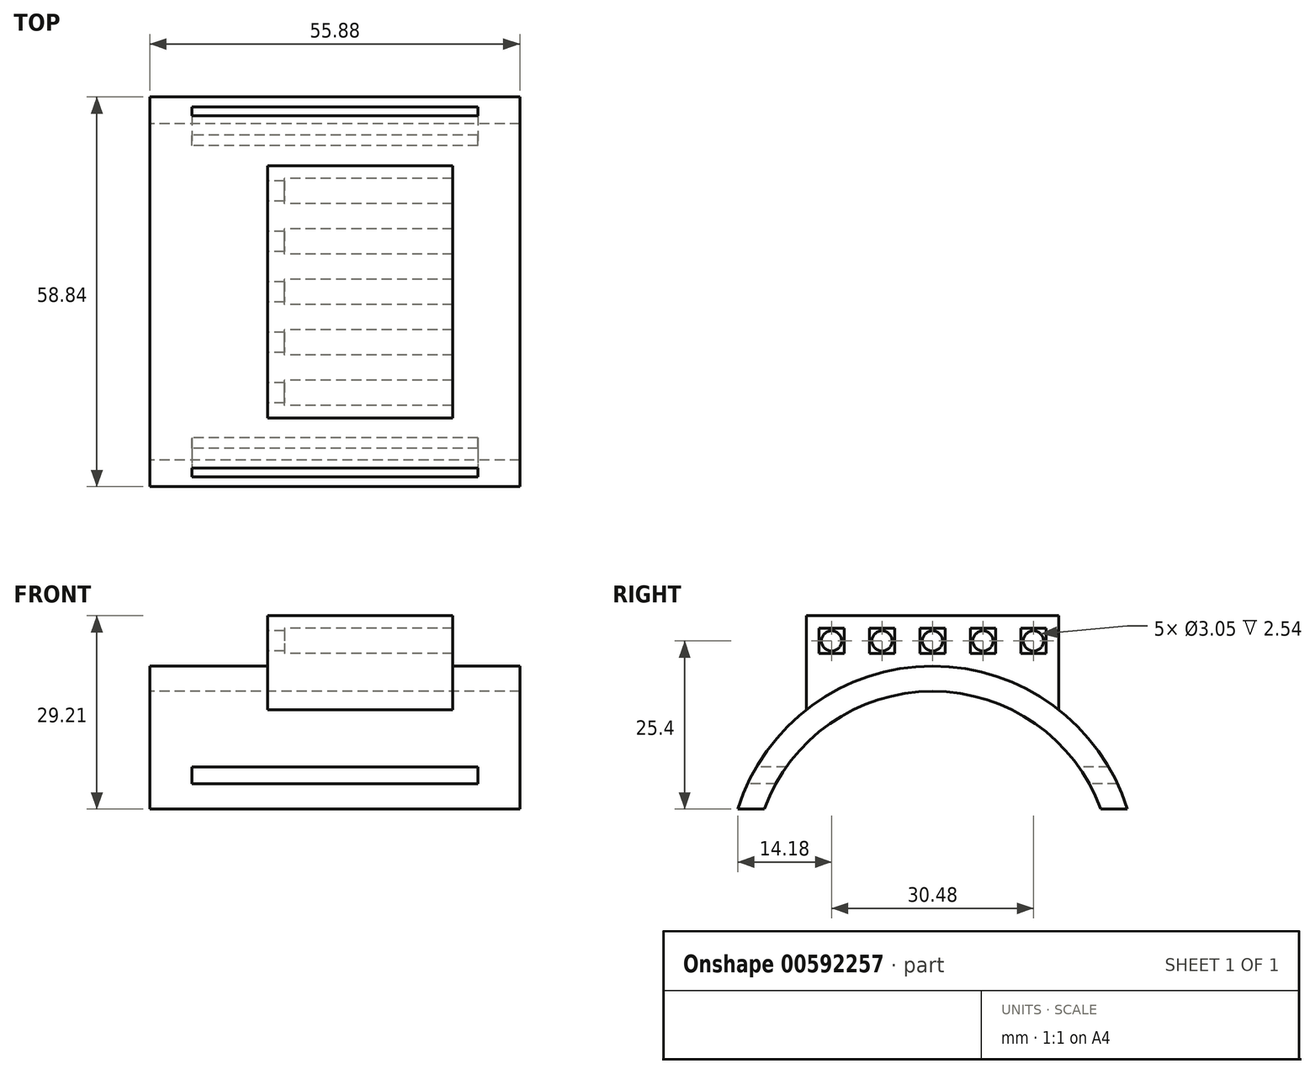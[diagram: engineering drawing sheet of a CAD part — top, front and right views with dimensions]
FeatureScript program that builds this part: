
annotation { "Feature Type Name" : "Feature", "Feature Type Description" : "" }
export const myFeature = defineFeature(function(context is Context, id is Id, definition is map)
    precondition{}
    {
        {
            var Q0;
            Q0=qCreatedBy(makeId("Right.planeOp"),FACE);
            var sketch = newSketch(context, id + "F0", { "sketchPlane" : qUnion([Q0])});
            skLineSegment(sketch, "E0", {"start": v(0, 0) * mm, "end": v(50.8, 0) * mm});
            skLineSegment(sketch, "E1", {"start": v(25.4, 0) * mm, "end": v(25.4, 17.78) * mm});
            skArc(sketch, "E2", {"start": v(50.8, 0) * mm, "mid": v(25.4, 17.78) * mm, "end": v(0, 0) * mm});
            skLineSegment(sketch, "E3", {"start": v(0, 0) * mm, "end": v(-4.02, 0) * mm});
            skLineSegment(sketch, "E4.MirrorCS", {"start": v(50.8, 0) * mm, "end": v(54.82, 0) * mm});
            skArc(sketch, "E5.0", {"start": v(54.82, 0) * mm, "mid": v(25.4, 21.6) * mm, "end": v(-4.02, 0) * mm});
            skPoint(sketch, "E6.orphan", {"position": v(-3.81, 0) * mm});
            skPoint(sketch, "E7.orphan", {"position": v(54.61, 0) * mm});
            skSolve(sketch);
        }
        {
            var Q0;
            {var subQ1=sQuery(id+"F0.wireOp",EDGE,"E3");Q0=makeQuery(id+"F0.imprint","IMPRINT",FACE,{"disambiguationData":[TD([[makeQuery(id+"F0.imprint","IMPRINT",EDGE,{"derivedFrom":subQ1}),-1.0]])]});}
            extrude(context, id + "F1", {"entities" : qUnion([Q0]), "depth" : 55.88 * mm, "offsetDistance" : 25.4 * mm});
        }
        {
            var Q0;
            Q0=makeQuery(id+"F1.opExtrude","CAP_FACE",FACE,{"disambiguationData":[OSD([sQuery(id+"F0.wireOp",EDGE,"E2"),sQuery(id+"F0.wireOp",EDGE,"E3"),sQuery(id+"F0.wireOp",EDGE,"E4.MirrorCS"),sQuery(id+"F0.wireOp",EDGE,"E5.0")])],"isStart":true});
            cPlane(context, id + "F2", {"entities" : qUnion([Q0]), "cplaneType" : CPlaneType.OFFSET, "offset" : 17.78 * mm, "oppositeDirection" : true, "width" : 152.4 * mm, "height" : 152.4 * mm});
        }
        {
            var Q0;
            Q0=qCreatedBy(id+"F2.planeOp",FACE);
            var sketch = newSketch(context, id + "F3", { "sketchPlane" : qUnion([Q0])});
            skLineSegment(sketch, "E8", {"start": v(0, 0) * mm, "end": v(-25.4, 0) * mm});
            skLineSegment(sketch, "E9", {"start": v(-25.4, 0) * mm, "end": v(-25.4, 21.59) * mm});
            skLineSegment(sketch, "E10", {"start": v(-25.4, 21.59) * mm, "end": v(-25.4, 29.21) * mm});
            skCircle(sketch, "E11", {"center": v(-25.4, 25.4) * mm, "radius": 1.52 * mm});
            skCircle(sketch, "E12.1.0.0", {"center": v(-17.78, 25.4) * mm, "radius": 1.52 * mm});
            skCircle(sketch, "E12.2.0.0", {"center": v(-10.16, 25.4) * mm, "radius": 1.52 * mm});
            skLineSegment(sketch, "E12.direction1", {"start": v(-25.4, 25.4) * mm, "end": v(-17.78, 25.4) * mm, "construction": true});
            skCircle(sketch, "E13.1.0.0", {"center": v(-33.02, 25.4) * mm, "radius": 1.52 * mm});
            skCircle(sketch, "E13.2.0.0", {"center": v(-40.64, 25.4) * mm, "radius": 1.52 * mm});
            skLineSegment(sketch, "E13.direction1", {"start": v(-25.4, 25.4) * mm, "end": v(-33.02, 25.4) * mm, "construction": true});
            skLineSegment(sketch, "E14", {"start": v(-6.35, 29.21) * mm, "end": v(-25.4, 29.21) * mm});
            skLineSegment(sketch, "E15", {"start": v(-6.35, 29.2) * mm, "end": v(-6.35, 13.97) * mm});
            skLineSegment(sketch, "E16", {"start": v(-6.35, 13.97) * mm, "end": v(-25.4, 13.97) * mm});
            skLineSegment(sketch, "E17.MirrorCS", {"start": v(-44.45, 13.97) * mm, "end": v(-25.4, 13.97) * mm});
            skLineSegment(sketch, "E18.MirrorCS", {"start": v(-44.45, 29.2) * mm, "end": v(-44.45, 13.97) * mm});
            skLineSegment(sketch, "E19.MirrorCS", {"start": v(-44.45, 29.21) * mm, "end": v(-25.4, 29.21) * mm});
            skArc(sketch, "E20", {"start": v(-6.35, 13.97) * mm, "mid": v(-25.4, 21.59) * mm, "end": v(-44.45, 13.97) * mm});
            skSolve(sketch);
        }
        {
            var Q0;
            Q0=makeQuery(id+"F3.imprint","IMPRINT",FACE,{"disambiguationData":[TD([[makeQuery(id+"F3.imprint","IMPRINT",EDGE,{"derivedFrom":sQuery(id+"F3.wireOp",EDGE,"E13.1.0.0")}),-1.0]])]});
            var Q1;
            Q1=makeQuery(id+"F3.imprint","IMPRINT",FACE,{"disambiguationData":[TD([[makeQuery(id+"F3.imprint","IMPRINT",EDGE,{"derivedFrom":sQuery(id+"F3.wireOp",EDGE,"E12.1.0.0")}),-1.0]])]});
            extrude(context, id + "F4", {"entities" : qUnion([Q0, Q1]), "operationType" : NewBodyOperationType.ADD, "oppositeDirection" : true, "depth" : 2.54 * mm, "offsetDistance" : 25.4 * mm});
        }
        {
            var Q0;
            Q0=qCreatedBy(makeId("Front.planeOp"),FACE);
            var sketch = newSketch(context, id + "F5", { "sketchPlane" : qUnion([Q0])});
            skLineSegment(sketch, "E21.bottom", {"start": v(6.35, 6.35) * mm, "end": v(49.53, 6.35) * mm});
            skLineSegment(sketch, "E21.top", {"start": v(6.35, 3.81) * mm, "end": v(49.53, 3.81) * mm});
            skLineSegment(sketch, "E21.left", {"start": v(6.35, 6.35) * mm, "end": v(6.35, 3.8) * mm});
            skLineSegment(sketch, "E21.right", {"start": v(49.53, 6.35) * mm, "end": v(49.53, 3.81) * mm});
            skSolve(sketch);
        }
        {
            var Q0;
            Q0 = qSketchRegion(id + "F5", true);
            extrude(context, id + "F6", {"entities" : qUnion([Q0]), "operationType" : NewBodyOperationType.REMOVE, "endBound" : BoundingType.THROUGH_ALL, "oppositeDirection" : true, "depth" : 25.4 * mm, "offsetDistance" : 25.4 * mm, "hasSecondDirection" : true, "secondDirectionOppositeDirection" : false, "secondDirectionDepth" : 25.4 * mm});
        }
        {
            var Q0;
            Q0=makeQuery(id+"F4.opExtrude","CAP_FACE",FACE,{"disambiguationData":[OSD([sQuery(id+"F3.wireOp",EDGE,"E11"),sQuery(id+"F3.wireOp",EDGE,"E12.1.0.0"),sQuery(id+"F3.wireOp",EDGE,"E12.2.0.0"),sQuery(id+"F3.wireOp",EDGE,"E13.1.0.0"),sQuery(id+"F3.wireOp",EDGE,"E13.2.0.0"),sQuery(id+"F3.wireOp",EDGE,"E14"),sQuery(id+"F3.wireOp",EDGE,"E15"),sQuery(id+"F3.wireOp",EDGE,"E16"),sQuery(id+"F3.wireOp",EDGE,"E17.MirrorCS"),sQuery(id+"F3.wireOp",EDGE,"E18.MirrorCS"),sQuery(id+"F3.wireOp",EDGE,"E19.MirrorCS")])],"isStart":false});
            var sketch = newSketch(context, id + "F7", { "sketchPlane" : qUnion([Q0])});
            skLineSegment(sketch, "E22.bottom", {"start": v(8.25, 27.3) * mm, "end": v(12.06, 27.3) * mm});
            skLineSegment(sketch, "E22.top", {"start": v(8.25, 23.5) * mm, "end": v(12.06, 23.5) * mm});
            skLineSegment(sketch, "E22.left", {"start": v(8.25, 27.3) * mm, "end": v(8.25, 23.5) * mm});
            skLineSegment(sketch, "E22.right", {"start": v(12.06, 27.3) * mm, "end": v(12.06, 23.5) * mm});
            skLineSegment(sketch, "E23.1.0.0", {"start": v(15.87, 27.3) * mm, "end": v(19.68, 27.3) * mm});
            skLineSegment(sketch, "E23.1.0.1", {"start": v(15.87, 23.5) * mm, "end": v(19.68, 23.5) * mm});
            skLineSegment(sketch, "E23.1.0.2", {"start": v(19.68, 27.3) * mm, "end": v(19.68, 23.5) * mm});
            skLineSegment(sketch, "E23.1.0.3", {"start": v(15.87, 27.3) * mm, "end": v(15.87, 23.5) * mm});
            skLineSegment(sketch, "E23.2.0.0", {"start": v(23.5, 27.3) * mm, "end": v(27.3, 27.3) * mm});
            skLineSegment(sketch, "E23.2.0.1", {"start": v(23.5, 23.5) * mm, "end": v(27.3, 23.5) * mm});
            skLineSegment(sketch, "E23.2.0.2", {"start": v(27.3, 27.3) * mm, "end": v(27.3, 23.5) * mm});
            skLineSegment(sketch, "E23.2.0.3", {"start": v(23.5, 27.3) * mm, "end": v(23.5, 23.5) * mm});
            skLineSegment(sketch, "E23.3.0.0", {"start": v(31.11, 27.3) * mm, "end": v(34.92, 27.3) * mm});
            skLineSegment(sketch, "E23.3.0.1", {"start": v(31.11, 23.5) * mm, "end": v(34.92, 23.5) * mm});
            skLineSegment(sketch, "E23.3.0.2", {"start": v(34.92, 27.3) * mm, "end": v(34.92, 23.5) * mm});
            skLineSegment(sketch, "E23.3.0.3", {"start": v(31.11, 27.3) * mm, "end": v(31.11, 23.5) * mm});
            skLineSegment(sketch, "E23.4.0.0", {"start": v(38.73, 27.3) * mm, "end": v(42.54, 27.3) * mm});
            skLineSegment(sketch, "E23.4.0.1", {"start": v(38.73, 23.5) * mm, "end": v(42.54, 23.5) * mm});
            skLineSegment(sketch, "E23.4.0.2", {"start": v(42.54, 27.3) * mm, "end": v(42.54, 23.5) * mm});
            skLineSegment(sketch, "E23.4.0.3", {"start": v(38.73, 27.3) * mm, "end": v(38.73, 23.5) * mm});
            skLineSegment(sketch, "E23.direction1", {"start": v(8.25, 23.5) * mm, "end": v(15.87, 23.5) * mm, "construction": true});
            skSolve(sketch);
        }
        {
            var Q0;
            {var subQ72=sQuery(id+"F3.wireOp",EDGE,"E15");Q0=makeQuery(id+"F7.imprint","IMPRINT",FACE,{"disambiguationData":[TD([[makeQuery(id+"F7.imprint","IMPRINT",EDGE,{"derivedFrom":makeQuery(id+"F4.opExtrude","CAP_EDGE",EDGE,{"disambiguationData":[OSD([subQ72])],"isStart":false})}),1.0]])]});}
            extrude(context, id + "F8", {"entities" : qUnion([Q0]), "operationType" : NewBodyOperationType.ADD, "depth" : 25.4 * mm, "offsetDistance" : 25.4 * mm});
        }
    });
